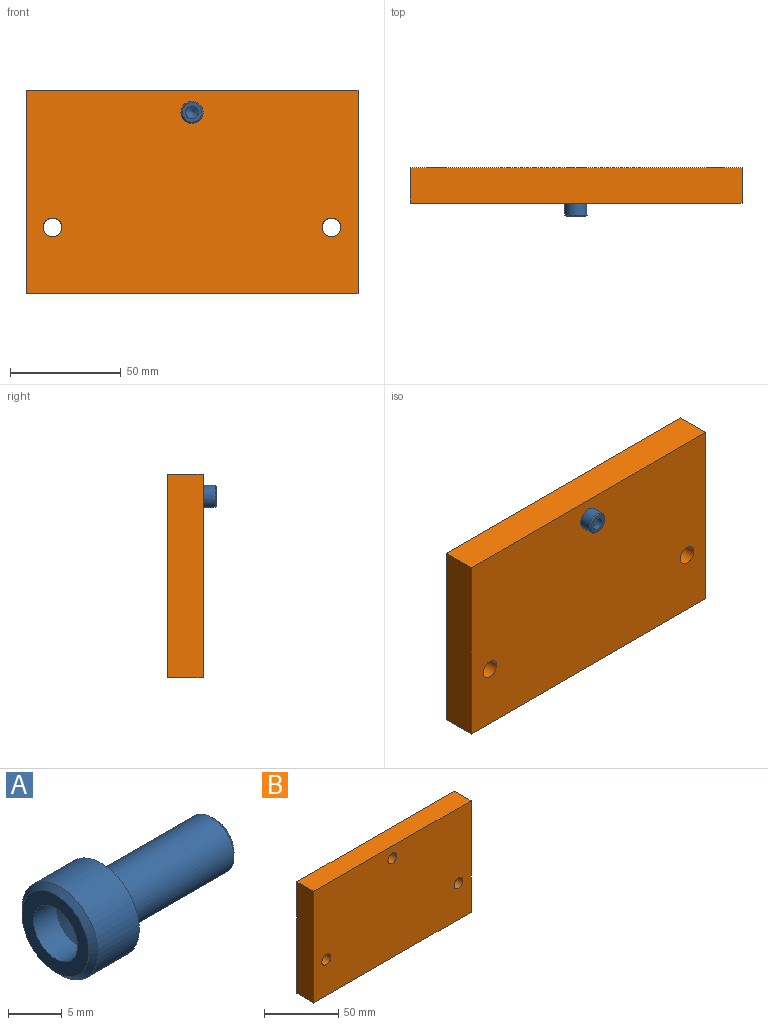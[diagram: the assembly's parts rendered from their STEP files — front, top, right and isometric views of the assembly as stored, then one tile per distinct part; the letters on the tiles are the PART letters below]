
ASSEMBLY  parts=2 mates=1
PART A: 9 faces, bbox 21x10x10 mm
  f0: plane 4.9x4.9mm, normal (1,0,0), area 18.9mm2, adj f1
  f1: cone r=3mm half-angle=45deg, axis (-1,0,0), area 13.3mm2, adj f0,f2
  f2: cylinder r=3mm len=14.45mm, axis (-1,0,0), area 272.4mm2, adj f1,f3
  f3: plane 10x10mm, normal (1,0,0), area 50.3mm2, adj f2,f4
  f4: cylinder r=5mm len=10mm, axis (-1,0,0), area 169.6mm2, adj f3,f5
  f5: cone r=5mm half-angle=45deg, axis (1,0,0), area 25.1mm2, adj f4,f6
  f6: plane 8.8x8.8mm, normal (-1,0,0), area 34.6mm2, adj f5,f7
  f7: cylinder r=2.89mm len=5.77mm, axis (-1,0,0), area 54.4mm2, adj f6,f8
  f8: cone r=2.89mm half-angle=60deg, axis (-1,0,0), area 30.2mm2, adj f7
PART B: 9 faces, bbox 150x16x92 mm
  f0: plane 150x92mm, normal (0,1,0), area 13629.8mm2, adj f1,f3,f4,f5,f6,f7,f8
  f1: plane 92x16mm, normal (-1,0,0), area 1472mm2, adj f0,f2,f4,f5
  f2: plane 150x92mm, normal (0,-1,0), area 13629.8mm2, adj f1,f3,f4,f5,f6,f7,f8
  f3: plane 92x16mm, normal (1,0,0), area 1472mm2, adj f0,f2,f4,f5
  f4: plane 150x16mm, normal (0,0,1), area 2400mm2, adj f0,f1,f2,f3
  f5: plane 150x16mm, normal (0,0,-1), area 2400mm2, adj f0,f1,f2,f3
  f6: cylinder r=4.25mm len=16mm, axis (0,-1,0), area 427.3mm2, adj f0,f2
  f7: cylinder r=4.25mm len=16mm, axis (0,-1,0), area 427.3mm2, adj f0,f2
  f8: cylinder r=4.25mm len=16mm, axis (0,-1,0), area 427.3mm2, adj f0,f2
PLACE A rot(axis=(-0.58,-0.58,0.58),120deg) t=(71.83,-18.41,59.57)mm
PLACE B t=(-3.17,-12.78,-22.43)mm
MATE fastened A.f1 <-> B.f6  axis (0,-1,0) through (71.83,-12.78,59.57)mm
